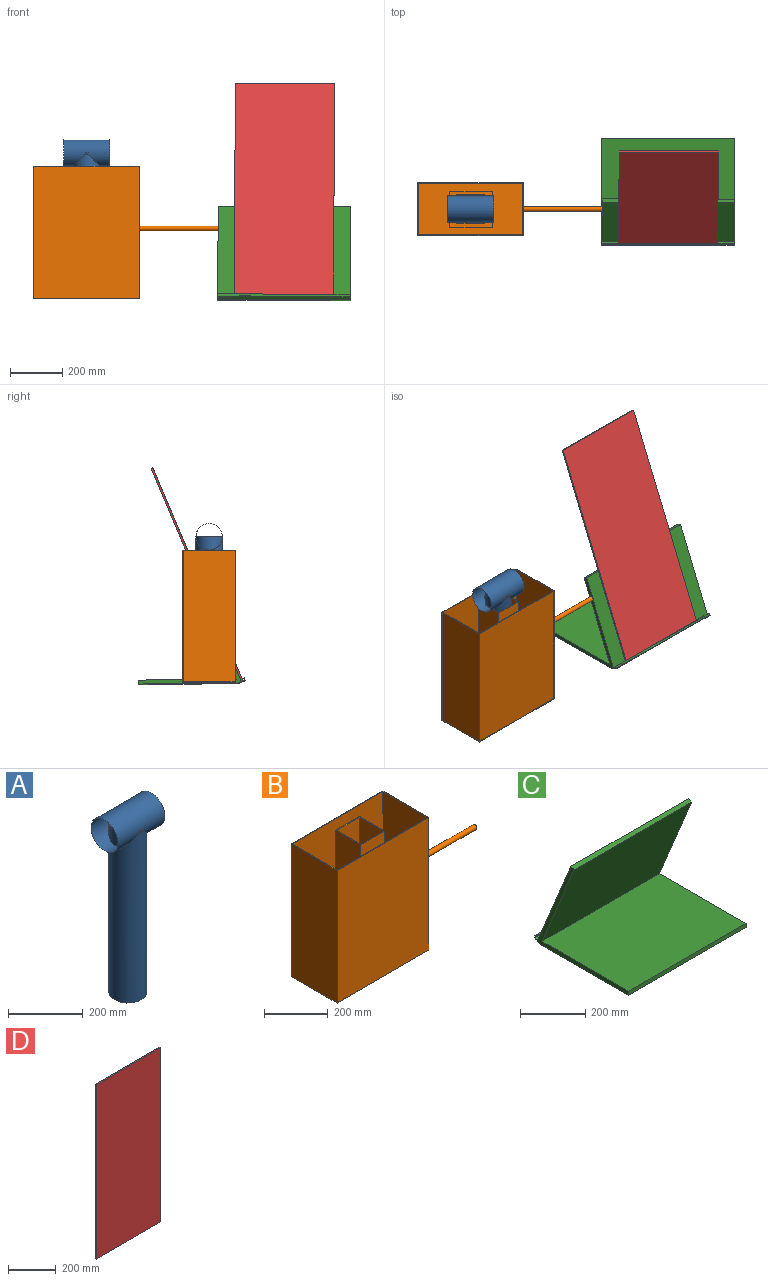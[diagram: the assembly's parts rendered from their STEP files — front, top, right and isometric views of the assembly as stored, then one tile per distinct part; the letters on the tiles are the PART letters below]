
ASSEMBLY  parts=4 mates=2
PART A: 10 faces, bbox 177.8x102.1x609.9 mm
  f0: plane 102.11x102.11mm, normal (1,0,0), area 81.3mm2, adj f2,f3
  f1: plane 102.11x102.11mm, normal (-1,0,0), area 81.3mm2, adj f2,f3
  f2: cylinder r=51.05mm len=177.8mm, axis (-1,0,0), area 46833.5mm2, adj f0,f1,f8
  f3: cylinder r=50.8mm len=177.8mm, axis (-1,0,0), area 46428.7mm2, adj f0,f1,f4,f6
  f4: cylinder r=50.8mm len=101.6mm, axis (0,0,1), area 5161.3mm2, adj f3,f5
  f5: plane 101.6x101.6mm, normal (0,0,1), area 790.5mm2, adj f4,f6,f9
  f6: cylinder r=50.8mm len=101.6mm, axis (0,0,1), area 5161.3mm2, adj f3,f5
  f7: plane 101.6x101.6mm, normal (0,0,-1), area 790.5mm2, adj f8,f9
  f8: cylinder r=50.8mm len=553.73mm, axis (0,0,1), area 167813.4mm2, adj f2,f7
  f9: cylinder r=48.26mm len=558.8mm, axis (0,0,1), area 169443mm2, adj f5,f7
PART B: 28 faces, bbox 711.2x203.2x508 mm
  f0: plane 406.4x203.2mm, normal (0,0,1), area 3071mm2, adj f4,f5,f6,f7,f14,f15,f16,f17
  f1: plane 508x107.52mm, normal (1,0,0), area 54621.5mm2, adj f2,f8,f9,f25
  f2: plane 508x101.4mm, normal (0,-1,0), area 51509.6mm2, adj f1,f3,f9,f25
  f3: plane 508x107.52mm, normal (-1,0,0), area 54621.5mm2, adj f2,f8,f9,f25
  f4: plane 508x203.2mm, normal (1,0,0), area 102977.3mm2, adj f0,f5,f7,f10,f26
  f5: plane 508x406.4mm, normal (0,1,0), area 206451.2mm2, adj f0,f4,f6,f10
  f6: plane 508x203.2mm, normal (-1,0,0), area 103225.6mm2, adj f0,f5,f7,f10
  f7: plane 508x406.4mm, normal (0,-1,0), area 206451.2mm2, adj f0,f4,f6,f10
  f8: plane 508x101.4mm, normal (0,1,0), area 51509.6mm2, adj f1,f3,f9,f25
  f9: plane 112.6x106.48mm, normal (0,0,1), area 1087.1mm2, adj f1,f2,f3,f8,f11,f12,f13,f18
  f10: plane 406.4x203.2mm, normal (0,0,-1), area 59972.4mm2, adj f4,f5,f6,f7,f21,f22,f23,f24
  f11: plane 505.46x112.6mm, normal (-1,0,0), area 56916.2mm2, adj f9,f12,f18,f19
  f12: plane 505.46x106.48mm, normal (0,1,0), area 53819.8mm2, adj f9,f11,f13,f19
  f13: plane 505.46x112.6mm, normal (1,0,0), area 56916.2mm2, adj f9,f12,f18,f19
  f14: plane 505.46x198.12mm, normal (-1,0,0), area 100141.7mm2, adj f0,f15,f17,f19
  f15: plane 505.46x401.32mm, normal (0,-1,0), area 202851.2mm2, adj f0,f14,f16,f19
  f16: plane 505.46x198.12mm, normal (1,0,0), area 100141.7mm2, adj f0,f15,f17,f19
  f17: plane 505.46x401.32mm, normal (0,1,0), area 202851.2mm2, adj f0,f14,f16,f19
  f18: plane 505.46x106.48mm, normal (0,-1,0), area 53819.8mm2, adj f9,f11,f13,f19
  f19: plane 401.32x198.12mm, normal (0,0,1), area 67519.9mm2, adj f11,f12,f13,f14,f15,f16,f17,f18
  f20: plane 162.8x138.87mm, normal (0,0,-1), area 22608.1mm2, adj f21,f22,f23,f24
  f21: plane 162.8x0mm, normal (0,1,0), area 0mm2, adj f10,f20
  f22: plane 138.87x0mm, normal (-1,0,0), area 0mm2, adj f10,f20
  f23: plane 162.8x0mm, normal (0,-1,0), area 0mm2, adj f10,f20
  f24: plane 138.87x0mm, normal (1,0,0), area 0mm2, adj f10,f20
  f25: plane 107.52x101.4mm, normal (0,0,1), area 10902.5mm2, adj f1,f2,f3,f8
  f26: cylinder r=8.89mm len=304.8mm, axis (-1,0,0), area 17025.4mm2, adj f4,f27
  f27: plane 17.78x17.78mm, normal (1,0,0), area 248.3mm2, adj f26
PART C: 13 faces, bbox 508x409.2x358 mm
  f0: plane 508x374.71mm, normal (0,0,1), area 190353.4mm2, adj f1,f10,f11,f12
  f1: plane 508x15.24mm, normal (0,-1,0), area 7741.9mm2, adj f0,f2,f11,f12
  f2: plane 508x381mm, normal (0,0,-1), area 193548mm2, adj f1,f3,f11,f12
  f3: plane 508x28.18mm, normal (0,0.38,-0.92), area 15483.8mm2, adj f2,f4,f11,f12
  f4: plane 508x8.48mm, normal (0,0.92,0.38), area 4658mm2, adj f3,f5,f11,f12
  f5: plane 508x2.02mm, normal (0,-0.38,0.92), area 1111mm2, adj f4,f6,f11,f12
  f6: plane 508x7.04mm, normal (0,-0.92,-0.38), area 3871mm2, adj f5,f7,f11,f12
  f7: plane 508x12.07mm, normal (0,-0.38,0.92), area 6630.9mm2, adj f6,f8,f11,f12
  f8: plane 508x350.76mm, normal (0,0.92,0.38), area 192761mm2, adj f7,f9,f11,f12
  f9: plane 508x14.09mm, normal (0,-0.38,0.92), area 7741.9mm2, adj f8,f10,f11,f12
  f10: plane 508x336.95mm, normal (0,-0.92,-0.38), area 185172.9mm2, adj f0,f9,f11,f12
  f11: plane 409.18x358.01mm, normal (1,0,0), area 11605.2mm2, adj f0,f1,f2,f3,f4,f5,f6,f7
  f12: plane 409.18x358.01mm, normal (-1,0,0), area 11605.2mm2, adj f0,f1,f2,f3,f4,f5,f6,f7
PART D: 6 faces, bbox 381x6.4x889 mm
  f0: plane 889x6.35mm, normal (1,0,0), area 5645.2mm2, adj f1,f3,f4,f5
  f1: plane 381x6.35mm, normal (0,0,1), area 2419.3mm2, adj f0,f2,f4,f5
  f2: plane 889x6.35mm, normal (-1,0,0), area 5645.2mm2, adj f1,f3,f4,f5
  f3: plane 381x6.35mm, normal (0,0,-1), area 2419.3mm2, adj f0,f2,f4,f5
  f4: plane 889x381mm, normal (0,-1,0), area 338709mm2, adj f0,f1,f2,f3
  f5: plane 889x381mm, normal (0,1,0), area 338709mm2, adj f0,f1,f2,f3
PLACE A t=(-77.68,-1003.9,706.64)mm
PLACE B t=(-78.55,-1004,147.84)mm fixed
PLACE C rot(axis=(0,0,1),179.9deg) t=(935.12,-978.23,464.91)mm fixed
PLACE D rot(axis=(1,0,0),157deg) t=(681.82,-939.06,612.94)mm
MATE fastened A.f4 <-> B.f25  axis (0,0,1) through (-77.68,-1003.9,147.84)mm
MATE fastened C.f8 <-> D.f4  axis (0,-0.92,0.39) through (679.48,-1127.78,151.21)mm
